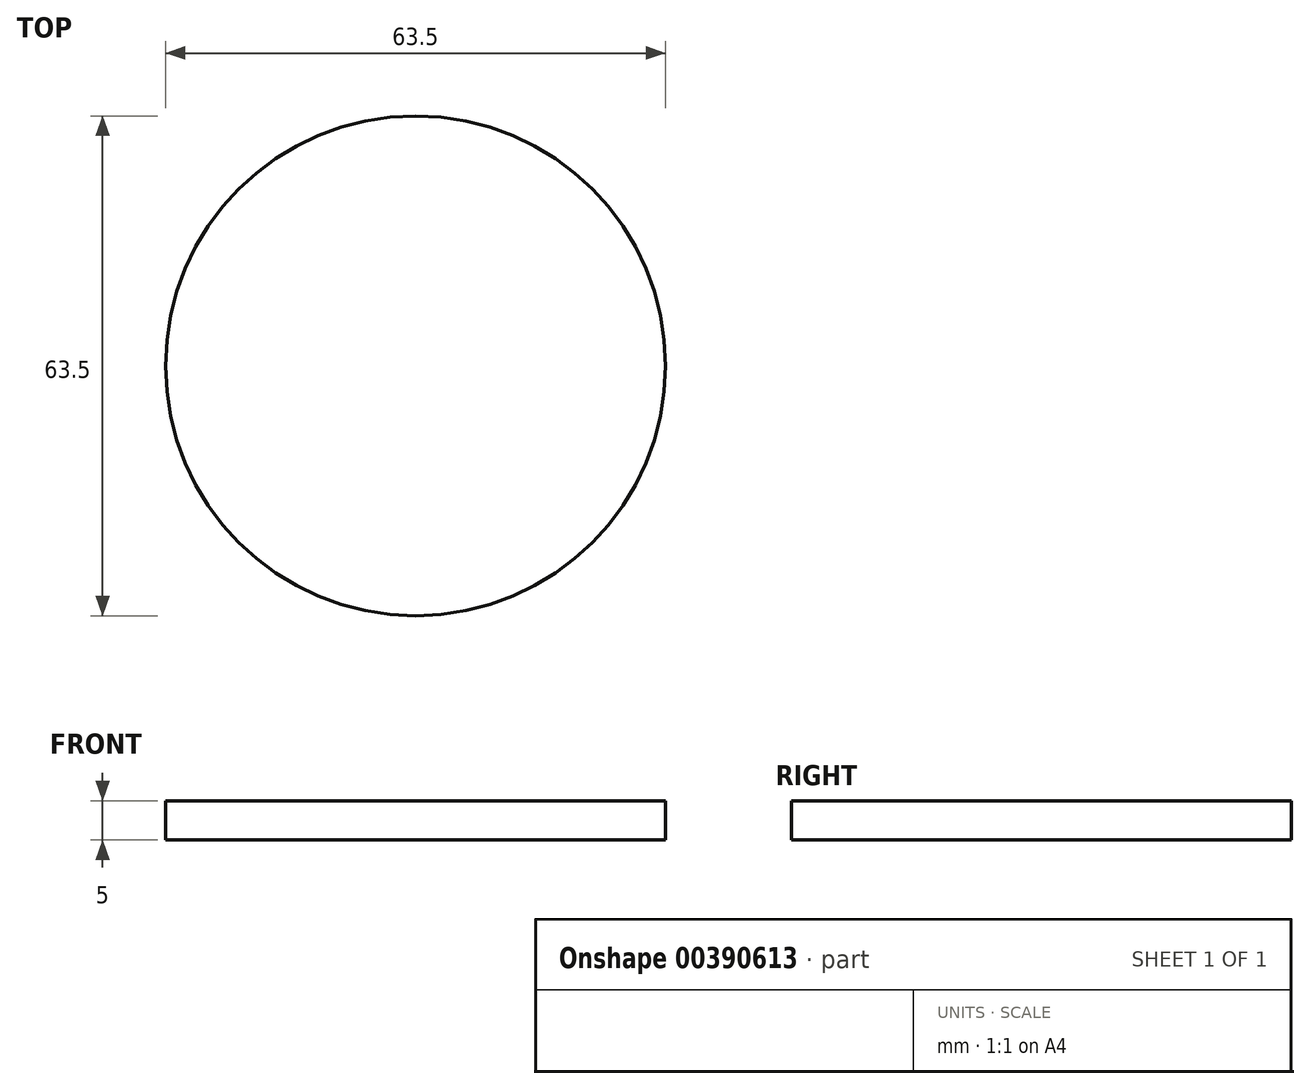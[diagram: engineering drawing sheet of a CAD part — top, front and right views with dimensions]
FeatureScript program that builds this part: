
annotation { "Feature Type Name" : "Feature", "Feature Type Description" : "" }
export const myFeature = defineFeature(function(context is Context, id is Id, definition is map)
    precondition{}
    {
        {
            var Q0;
            Q0=qCreatedBy(makeId("Top.planeOp"),FACE);
            var sketch = newSketch(context, id + "F0", { "sketchPlane" : qUnion([Q0])});
            skCircle(sketch, "E0", {"center": v(0, 0) * mm, "radius": 30.5 * mm});
            skCircle(sketch, "E1", {"center": v(0, 0) * mm, "radius": 31.75 * mm});
            skSolve(sketch);
        }
        {
            var Q0;
            Q0=makeQuery(id+"F0.imprint","IMPRINT",FACE,{"disambiguationData":[TD([[makeQuery(id+"F0.imprint","IMPRINT",EDGE,{"derivedFrom":sQuery(id+"F0.wireOp",EDGE,"E0")}),-1.0]])]});
            var Q1;
            Q1=makeQuery(id+"F0.imprint","IMPRINT",FACE,{"disambiguationData":[TD([[makeQuery(id+"F0.imprint","IMPRINT",EDGE,{"derivedFrom":sQuery(id+"F0.wireOp",EDGE,"E0")}),1.0]])]});
            extrude(context, id + "F1", {"entities" : qUnion([Q0, Q1]), "depth" : 5 * mm});
        }
    });
